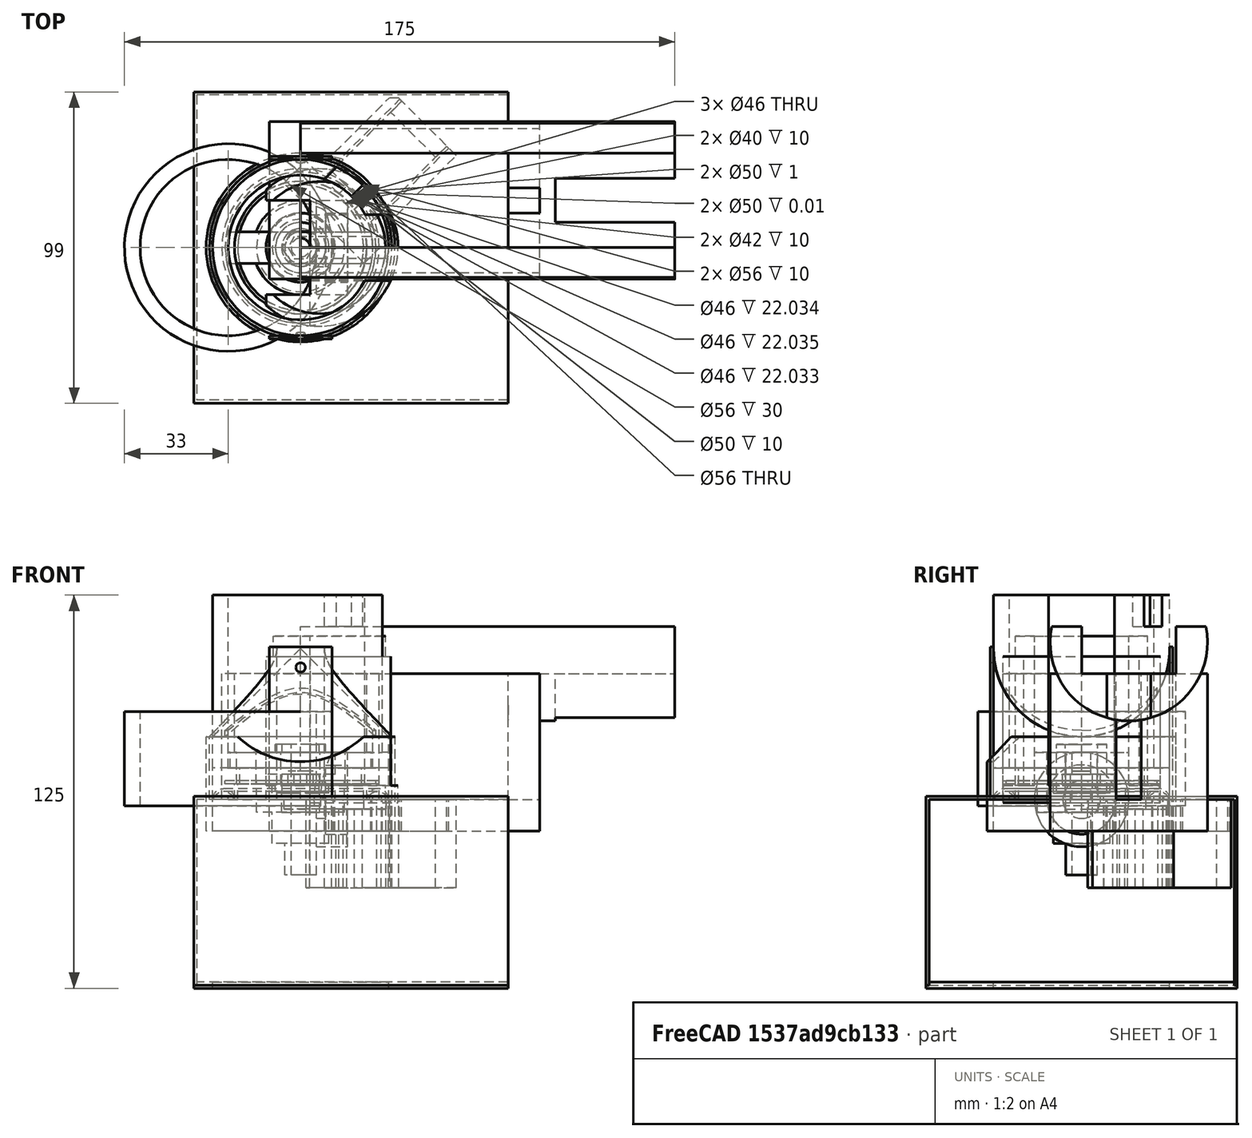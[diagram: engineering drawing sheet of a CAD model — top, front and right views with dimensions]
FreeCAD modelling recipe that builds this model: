
FCSTD DOCUMENT  (FreeCAD 0.18R16093 (Git))
Label: chess-robot-arm
License: All rights reserved
LicenseURL: http://en.wikipedia.org/wiki/All_rights_reserved
objects: Part::Cut×121, Part::Cylinder×116, Part::Box×52, Part::MultiFuse×35, App::DocumentObjectGroup×16, Part::RegularPolygon×9, Part::Extrusion×9, Part::MultiCommon×8, Part::Torus×7, App::MeasureDistance×2
note: 357 computed .brp shape members not serialized (recipe doc carries the construction recipe); baked Part::Feature solids carry a one-line shape summary decoded from their .brp

FEATURE [Part::Cylinder] Cylinder
  Angle = 360
  AttacherType = Attacher::AttachEngine3D
  Height = 10
  Radius = 29
FEATURE [Part::Torus] Torus
  Angle1 = -180
  Angle2 = 180
  Angle3 = 360
  AttacherType = Attacher::AttachEngine3D
  Placement = pos=(0,0,-1) rot=(0,0,1;0rad)
  Radius1 = 24.5
  Radius2 = 3.5
FEATURE [Part::Cut] Cut
  Base = -> Cylinder
  Tool = -> Torus
FEATURE [Part::Cylinder] Cylinder001
  Angle = 360
  AttacherType = Attacher::AttachEngine3D
  Height = 10
  Radius = 20
FEATURE [Part::Cut] Cut001
  Base = -> Cut
  Tool = -> Cylinder001
FEATURE [App::MeasureDistance] Distance  label="Distance: 87.82 mm"
  Distance = 87.8199
  P1 = (43.8613,-2.29371,0)
  P2 = (-43.9472,-0.873052,0)
FEATURE [App::MeasureDistance] Distance001  label="Distance: 10.00 mm"
  Distance = 10
  P1 = (30,0,0)
  P2 = (20,0,0)
FEATURE [Part::Cylinder] Cylinder002
  Angle = 360
  AttacherType = Attacher::AttachEngine3D
  Height = 10
  Radius = 23
FEATURE [Part::Box] Box  label="Cube"
  AttacherType = Attacher::AttachEngine3D
  Height = 10
  Length = 60
  Placement = pos=(-30,-5,0) rot=(0,0,1;0rad)
  Width = 10
FEATURE [Part::MultiCommon] Common  label="bolt-shaft"
  Shapes = -> [Box,Cylinder002]
FEATURE [Part::RegularPolygon] RegularPolygon  label="Regular polygon"
  AttacherType = Attacher::AttachEngine3D
  Circumradius = 6
  Polygon = 6
FEATURE [Part::Extrusion] Extrude  label="hex-head"
  Base = -> RegularPolygon
  Dir = (0,0,1)
  DirMode = 2
  FaceMakerClass = Part::FaceMakerBullseye
  LengthFwd = 3
  LengthRev = 0
  Solid = true
  Symmetric = false
FEATURE [Part::Cut] Cut002  label="bolt"
  Base = -> Common
  Tool = -> Extrude
FEATURE [Part::Cylinder] Cylinder003
  Angle = 360
  AttacherType = Attacher::AttachEngine3D
  Height = 10
  Radius = 3
FEATURE [Part::Cut] Cut003  label="center-axis001"
  Base = -> Cut002
  Placement = pos=(0,0,5) rot=(0,0,1;0rad)
  Tool = -> Cylinder003
FEATURE [Part::Cylinder] Cylinder004
  Angle = 360
  AttacherType = Attacher::AttachEngine3D
  Height = 0.01
  Placement = pos=(10,0,0) rot=(0,0,1;0rad)
  Radius = 24
FEATURE [Part::Cylinder] Cylinder005
  Angle = 360
  AttacherType = Attacher::AttachEngine3D
  Height = 0.01
  Placement = pos=(10,0,0) rot=(0,0,1;0rad)
  Radius = 25
FEATURE [Part::Cut] Cut004
  Base = -> Cylinder005
  Placement = pos=(-10,0,5) rot=(0,0,1;0rad)
  Tool = -> Cylinder004
FEATURE [Part::MultiFuse] Fusion
  Shapes = -> [Cut003,Cut001]
FEATURE [Part::Cut] Cut005  label="small-attachment001"
  Base = -> Fusion
  Tool = -> Cut004
FEATURE [Part::Torus] Torus001
  Angle1 = -180
  Angle2 = 180
  Angle3 = 360
  AttacherType = Attacher::AttachEngine3D
  Placement = pos=(0,0,-0.5) rot=(0,0,1;0rad)
  Radius1 = 24.5
  Radius2 = 3.5
FEATURE [Part::Cylinder] Cylinder006
  Angle = 360
  AttacherType = Attacher::AttachEngine3D
  Height = 10
  Radius = 20
FEATURE [Part::Cylinder] Cylinder007
  Angle = 360
  AttacherType = Attacher::AttachEngine3D
  Height = 10
  Radius = 29
FEATURE [Part::Cut] Cut007
  Base = -> Cylinder007
  Tool = -> Torus001
FEATURE [Part::Cut] Cut006
  Base = -> Cut007
  Tool = -> Cylinder006
FEATURE [Part::Cylinder] Cylinder008
  Angle = 360
  AttacherType = Attacher::AttachEngine3D
  Height = 1
  Placement = pos=(10,0,0) rot=(0,0,1;0rad)
  Radius = 25
FEATURE [Part::Cylinder] Cylinder009
  Angle = 360
  AttacherType = Attacher::AttachEngine3D
  Height = 10
  Radius = 23
FEATURE [Part::Box] Box001  label="Cube001"
  AttacherType = Attacher::AttachEngine3D
  Height = 10
  Length = 60
  Placement = pos=(-30,-5,0) rot=(0,0,1;0rad)
  Width = 10
FEATURE [Part::Cylinder] Cylinder010
  Angle = 360
  AttacherType = Attacher::AttachEngine3D
  Height = 5
  Placement = pos=(10,0,0) rot=(0,0,1;0rad)
  Radius = 24
FEATURE [Part::Cut] Cut008
  Base = -> Cylinder008
  Placement = pos=(-10,0,5) rot=(0,1,0;0rad)
  Tool = -> Cylinder010
FEATURE [Part::Cylinder] Cylinder011
  Angle = 360
  AttacherType = Attacher::AttachEngine3D
  Height = 10
  Radius = 3
FEATURE [Part::MultiCommon] Common001  label="bolt-shaft001"
  Shapes = -> [Box001,Cylinder009]
FEATURE [Part::RegularPolygon] RegularPolygon001  label="Regular polygon001"
  AttacherType = Attacher::AttachEngine3D
  Circumradius = 4
  Polygon = 6
FEATURE [Part::Extrusion] Extrude001  label="hex-head001"
  Base = -> RegularPolygon001
  Dir = (0,0,1)
  DirMode = 2
  FaceMakerClass = Part::FaceMakerBullseye
  LengthFwd = 4
  LengthRev = 0
  Solid = true
  Symmetric = false
FEATURE [Part::Cut] Cut011  label="bolt001"
  Base = -> Common001
  Tool = -> Extrude001
FEATURE [Part::Cut] Cut009  label="center-axis002"
  Base = -> Cut011
  Placement = pos=(0,0,5) rot=(0,0,1;0rad)
  Tool = -> Cylinder011
FEATURE [Part::MultiFuse] Fusion001
  Shapes = -> [Cut009,Cut006]
FEATURE [Part::Cut] Cut010
  Base = -> Fusion001
  Tool = -> Cut008
FEATURE [Part::Cylinder] Cylinder012  label="center-Cylinder012"
  Angle = 360
  AttacherType = Attacher::AttachEngine3D
  Height = 10
  Placement = pos=(0,0,5) rot=(0,0,1;0rad)
  Radius = 15
FEATURE [Part::Cylinder] Cylinder013
  Angle = 360
  AttacherType = Attacher::AttachEngine3D
  Height = 38
  Radius = 28
FEATURE [Part::Cylinder] Cylinder014
  Angle = 360
  AttacherType = Attacher::AttachEngine3D
  Height = 38
  Radius = 23
FEATURE [Part::Cut] Cut012
  Base = -> Cylinder013
  Tool = -> Cylinder014
FEATURE [Part::Cylinder] Cylinder015
  Angle = 360
  AttacherType = Attacher::AttachEngine3D
  Height = 61
  Placement = pos=(-29,0,38) rot=(0,1,0;1.5708rad)
  Radius = 28
FEATURE [Part::Cut] Cut013
  Base = -> Cut012
  Tool = -> Cylinder015
FEATURE [Part::Cylinder] Cylinder016
  Angle = 360
  AttacherType = Attacher::AttachEngine3D
  Height = 40
  Radius = 23
FEATURE [Part::Cylinder] Cylinder017
  Angle = 360
  AttacherType = Attacher::AttachEngine3D
  Height = 61
  Placement = pos=(-29,0,40) rot=(0,1,0;1.5708rad)
  Radius = 28
FEATURE [Part::Cylinder] Cylinder018
  Angle = 360
  AttacherType = Attacher::AttachEngine3D
  Height = 40
  Radius = 24
FEATURE [Part::Cut] Cut014
  Base = -> Cylinder018
  Tool = -> Cylinder016
FEATURE [Part::Cut] Cut015
  Base = -> Cut014
  Tool = -> Cylinder017
FEATURE [Part::MultiFuse] Fusion002
  Placement = pos=(0,0,10) rot=(0,0,1;0rad)
  Shapes = -> [Cut015,Cut013]
FEATURE [App::DocumentObjectGroup] Group002  label="Servo bend"
  Group = -> [Fusion002]
FEATURE [Part::Cylinder] Cylinder019
  Angle = 360
  AttacherType = Attacher::AttachEngine3D
  Height = 48
  Radius = 23
FEATURE [Part::Cylinder] Cylinder020
  Angle = 360
  AttacherType = Attacher::AttachEngine3D
  Height = 61
  Placement = pos=(-29,0,38) rot=(0,1,0;1.5708rad)
  Radius = 28
FEATURE [Part::Cylinder] Cylinder021
  Angle = 360
  AttacherType = Attacher::AttachEngine3D
  Height = 48
  Radius = 29
FEATURE [Part::Cut] Cut016
  Base = -> Cylinder021
  Tool = -> Cylinder019
FEATURE [Part::Cut] Cut017
  Base = -> Cut016
  Tool = -> Cylinder020
FEATURE [Part::Cylinder] Cylinder022
  Angle = 360
  AttacherType = Attacher::AttachEngine3D
  Height = 40
  Radius = 23
FEATURE [Part::Cylinder] Cylinder023
  Angle = 360
  AttacherType = Attacher::AttachEngine3D
  Height = 61
  Placement = pos=(-29,0,40) rot=(0,1,0;1.5708rad)
  Radius = 28
FEATURE [Part::Cylinder] Cylinder024
  Angle = 360
  AttacherType = Attacher::AttachEngine3D
  Height = 40
  Radius = 24
FEATURE [Part::Cut] Cut018
  Base = -> Cylinder024
  Tool = -> Cylinder022
FEATURE [Part::Cut] Cut019
  Base = -> Cut018
  Tool = -> Cylinder023
FEATURE [Part::MultiFuse] Fusion003
  Placement = pos=(0,0,10) rot=(0,0,1;0rad)
  Shapes = -> [Cut019,Cut017]
FEATURE [Part::MultiFuse] Fusion004
  Shapes = -> [Cylinder012,Cut010]
FEATURE [Part::MultiFuse] Fusion005
  Shapes = -> [Fusion004,Fusion003]
FEATURE [Part::Cylinder] Cylinder025  label="center-Cylinder025"
  Angle = 360
  AttacherType = Attacher::AttachEngine3D
  Height = 7
  Placement = pos=(0,0,8) rot=(0,0,1;0rad)
  Radius = 11
FEATURE [Part::Cut] Cut020
  Base = -> Fusion005
  Tool = -> Cylinder025
FEATURE [Part::Cylinder] Cylinder026  label="center-Cylinder026"
  Angle = 360
  AttacherType = Attacher::AttachEngine3D
  Height = 10
  Placement = pos=(0,0,5) rot=(0,0,1;0rad)
  Radius = 6
FEATURE [Part::Cut] Cut021
  Base = -> Cut020
  Tool = -> Cylinder026
FEATURE [Part::Cylinder] Cylinder027
  Angle = 360
  AttacherType = Attacher::AttachEngine3D
  Height = 45
  Radius = 23
FEATURE [Part::Cylinder] Cylinder028
  Angle = 360
  AttacherType = Attacher::AttachEngine3D
  Height = 61
  Placement = pos=(-29,0,38) rot=(0,1,0;1.5708rad)
  Radius = 28
FEATURE [Part::Cylinder] Cylinder029
  Angle = 360
  AttacherType = Attacher::AttachEngine3D
  Height = 45
  Radius = 29
FEATURE [Part::Cut] Cut022
  Base = -> Cylinder029
  Tool = -> Cylinder027
FEATURE [Part::Cut] Cut023
  Base = -> Cut022
  Tool = -> Cylinder028
FEATURE [Part::Cylinder] Cylinder030
  Angle = 360
  AttacherType = Attacher::AttachEngine3D
  Height = 40
  Radius = 23
FEATURE [Part::Cylinder] Cylinder031
  Angle = 360
  AttacherType = Attacher::AttachEngine3D
  Height = 61
  Placement = pos=(-29,0,40) rot=(0,1,0;1.5708rad)
  Radius = 28
FEATURE [Part::Cylinder] Cylinder032
  Angle = 360
  AttacherType = Attacher::AttachEngine3D
  Height = 40
  Radius = 24
FEATURE [Part::Cut] Cut024
  Base = -> Cylinder032
  Tool = -> Cylinder030
FEATURE [Part::Cut] Cut025
  Base = -> Cut024
  Tool = -> Cylinder031
FEATURE [Part::MultiFuse] Fusion006
  Placement = pos=(0,0,10) rot=(0,0,1;0rad)
  Shapes = -> [Cut025,Cut023]
FEATURE [Part::MultiFuse] Fusion007
  Shapes = -> [Fusion006,Cut005]
FEATURE [Part::Cylinder] Cylinder033
  Angle = 360
  AttacherType = Attacher::AttachEngine3D
  Height = 53
  Placement = pos=(6,0,-1) rot=(0,0,1;0rad)
  Radius = 25
FEATURE [Part::Box] Box002  label="Cube002"
  AttacherType = Attacher::AttachEngine3D
  Height = 41
  Length = 50
  Placement = pos=(-15,-10.5,4.5) rot=(0,0,1;0rad)
  Width = 21
FEATURE [Part::Cut] Cut026
  Base = -> Cylinder033
  Tool = -> Box002
FEATURE [Part::Box] Box003  label="Cube003"
  AttacherType = Attacher::AttachEngine3D
  Height = 71
  Length = 55
  Placement = pos=(-66,-25,-15) rot=(0,0,1;0rad)
  Width = 56
FEATURE [Part::Cut] Cut027
  Base = -> Cut026
  Tool = -> Box003
FEATURE [Part::Box] Box004  label="Cube004"
  AttacherType = Attacher::AttachEngine3D
  Height = 7
  Length = 24
  Placement = pos=(3,-3.5,-1) rot=(0,0,1;0rad)
  Width = 7
FEATURE [Part::Cut] Cut028
  Base = -> Cut027
  Tool = -> Box004
FEATURE [Part::Cylinder] Cylinder034
  Angle = 360
  AttacherType = Attacher::AttachEngine3D
  Height = 5
  Radius = 3
FEATURE [Part::Cylinder] Cylinder035
  Angle = 360
  AttacherType = Attacher::AttachEngine3D
  Height = 5
  Radius = 11
FEATURE [Part::Cut] Cut029
  Base = -> Cylinder035
  Tool = -> Cylinder034
FEATURE [Part::Cylinder] Cylinder036
  Angle = 360
  AttacherType = Attacher::AttachEngine3D
  Height = 10
  Placement = pos=(0,0,4.5) rot=(0,0,1;0rad)
  Radius = 10.6
FEATURE [Part::Cut] Cut030
  Base = -> Cut029
  Tool = -> Cylinder036
FEATURE [App::DocumentObjectGroup] Group004  label="shaft-coupler"
  Group = -> [Cut030]
FEATURE [Part::Torus] Torus002
  Angle1 = -180
  Angle2 = 180
  Angle3 = 360
  AttacherType = Attacher::AttachEngine3D
  Radius1 = 24.5
  Radius2 = 3.5
FEATURE [Part::RegularPolygon] RegularPolygon002  label="Regular polygon002"
  AttacherType = Attacher::AttachEngine3D
  Circumradius = 4
  Polygon = 6
FEATURE [Part::Cylinder] Cylinder037
  Angle = 360
  AttacherType = Attacher::AttachEngine3D
  Height = 10
  Radius = 28
FEATURE [Part::Cylinder] Cylinder038
  Angle = 360
  AttacherType = Attacher::AttachEngine3D
  Height = 10
  Radius = 21
FEATURE [Part::Box] Box005  label="Cube005"
  AttacherType = Attacher::AttachEngine3D
  Height = 10
  Length = 60
  Placement = pos=(-30,-5,0) rot=(0,0,1;0rad)
  Width = 10
FEATURE [Part::Cylinder] Cylinder039
  Angle = 360
  AttacherType = Attacher::AttachEngine3D
  Height = 0.01
  Placement = pos=(10,0,0) rot=(0,0,1;0rad)
  Radius = 25
FEATURE [Part::Cylinder] Cylinder040
  Angle = 360
  AttacherType = Attacher::AttachEngine3D
  Height = 0.01
  Placement = pos=(10,0,0) rot=(0,0,1;0rad)
  Radius = 24
FEATURE [Part::Cylinder] Cylinder041
  Angle = 360
  AttacherType = Attacher::AttachEngine3D
  Height = 10
  Radius = 23
FEATURE [Part::MultiCommon] Common002  label="bolt-shaft002"
  Shapes = -> [Box005,Cylinder041]
FEATURE [Part::Cylinder] Cylinder042
  Angle = 360
  AttacherType = Attacher::AttachEngine3D
  Height = 10
  Radius = 3
FEATURE [Part::Extrusion] Extrude002  label="hex-head002"
  Base = -> RegularPolygon002
  Dir = (0,0,1)
  DirMode = 2
  FaceMakerClass = Part::FaceMakerBullseye
  LengthFwd = 4
  LengthRev = 0
  Solid = true
  Symmetric = false
FEATURE [Part::Cut] Cut032
  Base = -> Cylinder039
  Placement = pos=(-10,0,5) rot=(0,0,1;0rad)
  Tool = -> Cylinder040
FEATURE [Part::Cut] Cut034
  Base = -> Cylinder037
  Tool = -> Torus002
FEATURE [Part::Cut] Cut031
  Base = -> Cut034
  Tool = -> Cylinder038
FEATURE [Part::Cut] Cut036  label="bolt002"
  Base = -> Common002
  Tool = -> Extrude002
FEATURE [Part::Cut] Cut033  label="center-axis003"
  Base = -> Cut036
  Placement = pos=(0,0,5) rot=(0,0,1;0rad)
  Tool = -> Cylinder042
FEATURE [Part::MultiFuse] Fusion008
  Shapes = -> [Cut033,Cut031]
FEATURE [Part::Cut] Cut035  label="small-attachment-base"
  Base = -> Fusion008
  Tool = -> Cut032
FEATURE [Part::Cylinder] Cylinder043
  Angle = 360
  AttacherType = Attacher::AttachEngine3D
  Height = 10
  Radius = 28
FEATURE [Part::Cylinder] Cylinder044
  Angle = 360
  AttacherType = Attacher::AttachEngine3D
  Height = 10
  Radius = 21
FEATURE [Part::Torus] Torus003
  Angle1 = -180
  Angle2 = 180
  Angle3 = 360
  AttacherType = Attacher::AttachEngine3D
  Radius1 = 24.5
  Radius2 = 3.5
FEATURE [Part::RegularPolygon] RegularPolygon003  label="Regular polygon003"
  AttacherType = Attacher::AttachEngine3D
  Circumradius = 4
  Polygon = 6
FEATURE [Part::Extrusion] Extrude003  label="hex-head003"
  Base = -> RegularPolygon003
  Dir = (0,0,1)
  DirMode = 2
  FaceMakerClass = Part::FaceMakerBullseye
  LengthFwd = 4
  LengthRev = 0
  Solid = true
  Symmetric = false
FEATURE [Part::Cut] Cut042
  Base = -> Cylinder043
  Tool = -> Torus003
FEATURE [Part::Cut] Cut041
  Base = -> Cut042
  Tool = -> Cylinder044
FEATURE [Part::Box] Box006  label="Cube006"
  AttacherType = Attacher::AttachEngine3D
  Height = 10
  Length = 60
  Placement = pos=(-30,-5,0) rot=(0,0,1;0rad)
  Width = 10
FEATURE [Part::Cylinder] Cylinder045
  Angle = 360
  AttacherType = Attacher::AttachEngine3D
  Height = 5
  Placement = pos=(10,0,0) rot=(0,0,1;0rad)
  Radius = 24
FEATURE [Part::Cylinder] Cylinder046
  Angle = 360
  AttacherType = Attacher::AttachEngine3D
  Height = 10
  Radius = 23
FEATURE [Part::MultiCommon] Common003  label="bolt-shaft003"
  Shapes = -> [Box006,Cylinder046]
FEATURE [Part::Cut] Cut040  label="bolt003"
  Base = -> Common003
  Tool = -> Extrude003
FEATURE [Part::Cylinder] Cylinder047
  Angle = 360
  AttacherType = Attacher::AttachEngine3D
  Height = 10
  Radius = 3
FEATURE [Part::Cut] Cut038  label="center-axis004"
  Base = -> Cut040
  Placement = pos=(0,0,5) rot=(0,0,1;0rad)
  Tool = -> Cylinder047
FEATURE [Part::MultiFuse] Fusion009
  Shapes = -> [Cut038,Cut041]
FEATURE [Part::Cylinder] Cylinder048
  Angle = 360
  AttacherType = Attacher::AttachEngine3D
  Height = 1
  Placement = pos=(10,0,0) rot=(0,0,1;0rad)
  Radius = 25
FEATURE [Part::Cut] Cut037
  Base = -> Cylinder048
  Placement = pos=(-10,0,5) rot=(0,1,0;0rad)
  Tool = -> Cylinder045
FEATURE [Part::Cut] Cut039
  Base = -> Fusion009
  Tool = -> Cut037
FEATURE [Part::Cylinder] Cylinder049  label="center-Cylinder027"
  Angle = 360
  AttacherType = Attacher::AttachEngine3D
  Height = 10
  Placement = pos=(0,0,5) rot=(0,0,1;0rad)
  Radius = 15
FEATURE [Part::MultiFuse] Fusion010
  Shapes = -> [Cylinder049,Cut039]
FEATURE [Part::Cylinder] Cylinder050  label="center-Cylinder028"
  Angle = 360
  AttacherType = Attacher::AttachEngine3D
  Height = 7
  Placement = pos=(0,0,8) rot=(0,0,1;0rad)
  Radius = 11
FEATURE [Part::Cylinder] Cylinder051  label="center-Cylinder029"
  Angle = 360
  AttacherType = Attacher::AttachEngine3D
  Height = 10
  Placement = pos=(0,0,5) rot=(0,0,1;0rad)
  Radius = 6
FEATURE [Part::Cut] Cut043
  Base = -> Fusion010
  Tool = -> Cylinder050
FEATURE [Part::Cut] Cut044  label="large-attachement-base"
  Base = -> Cut043
  Tool = -> Cylinder051
FEATURE [Part::Cylinder] Cylinder052  label="Cylinder049"
  Angle = 360
  AttacherType = Attacher::AttachEngine3D
  Height = 30
  Placement = pos=(0,0,10) rot=(0,0,1;0rad)
  Radius = 21
FEATURE [Part::Cylinder] Cylinder053  label="Cylinder050"
  Angle = 360
  AttacherType = Attacher::AttachEngine3D
  Height = 30
  Placement = pos=(0,0,10) rot=(0,0,1;0rad)
  Radius = 25
FEATURE [Part::Cut] Cut045
  Base = -> Cylinder053
  Tool = -> Cylinder052
FEATURE [Part::MultiFuse] Fusion011
  Shapes = -> [Cut035,Cut045]
FEATURE [App::DocumentObjectGroup] Group005  label="robot base coupler"
  Group = -> [Fusion011]
FEATURE [Part::Cylinder] Cylinder054  label="Cylinder051"
  Angle = 360
  AttacherType = Attacher::AttachEngine3D
  Height = 55
  Placement = pos=(0,0,10) rot=(0,0,1;0rad)
  Radius = 23
FEATURE [Part::Cylinder] Cylinder055  label="Cylinder052"
  Angle = 360
  AttacherType = Attacher::AttachEngine3D
  Height = 55
  Placement = pos=(0,0,10) rot=(0,0,1;0rad)
  Radius = 28
FEATURE [Part::Cut] Cut046  label="touch-bottom"
  Base = -> Cylinder055
  Tool = -> Cylinder054
FEATURE [Part::MultiFuse] Fusion012
  Shapes = -> [Cut046,Cut044]
FEATURE [Part::Box] Box007  label="servo inlet"
  AttacherType = Attacher::AttachEngine3D
  Height = 55
  Length = 35
  Placement = pos=(0,-10.5,15) rot=(0,0,1;0rad)
  Width = 21
FEATURE [Part::Cut] Cut047
  Base = -> Fusion012
  Tool = -> Box007
FEATURE [Part::Box] Box008  label="cabel inlet"
  AttacherType = Attacher::AttachEngine3D
  Height = 10
  Length = 18
  Placement = pos=(10,10,55) rot=(0,0,1;0.785398rad)
  Width = 10
FEATURE [Part::Cut] Cut048  label="base"
  Base = -> Cut047
  Tool = -> Box008
FEATURE [App::DocumentObjectGroup] Group006  label="robot base"
  Group = -> [Cut048]
FEATURE [Part::Torus] Torus004
  Angle1 = -180
  Angle2 = 180
  Angle3 = 360
  AttacherType = Attacher::AttachEngine3D
  Radius1 = 25.5
  Radius2 = 2.5
FEATURE [Part::Cylinder] Cylinder056
  Angle = 360
  AttacherType = Attacher::AttachEngine3D
  Height = 10
  Radius = 23
FEATURE [Part::Cylinder] Cylinder057
  Angle = 360
  AttacherType = Attacher::AttachEngine3D
  Height = 5
  Placement = pos=(10,0,0) rot=(0,0,1;0rad)
  Radius = 24
FEATURE [Part::Cylinder] Cylinder058
  Angle = 360
  AttacherType = Attacher::AttachEngine3D
  Height = 10
  Radius = 28
FEATURE [Part::Box] Box009  label="Cube007"
  AttacherType = Attacher::AttachEngine3D
  Height = 10
  Length = 60
  Placement = pos=(-30,-5,0) rot=(0,0,1;0rad)
  Width = 10
FEATURE [Part::MultiCommon] Common004  label="bolt-shaft004"
  Shapes = -> [Box009,Cylinder056]
FEATURE [Part::Cylinder] Cylinder059
  Angle = 360
  AttacherType = Attacher::AttachEngine3D
  Height = 10
  Radius = 23
FEATURE [Part::Cut] Cut051
  Base = -> Cylinder058
  Tool = -> Torus004
FEATURE [Part::Cut] Cut058
  Base = -> Cut051
  Tool = -> Cylinder059
FEATURE [Part::RegularPolygon] RegularPolygon004  label="Regular polygon004"
  AttacherType = Attacher::AttachEngine3D
  Circumradius = 4
  Polygon = 6
FEATURE [Part::Extrusion] Extrude004  label="hex-head004"
  Base = -> RegularPolygon004
  Dir = (0,0,1)
  DirMode = 2
  FaceMakerClass = Part::FaceMakerBullseye
  LengthFwd = 4
  LengthRev = 0
  Solid = true
  Symmetric = false
FEATURE [Part::Cut] Cut056  label="bolt004"
  Base = -> Common004
  Tool = -> Extrude004
FEATURE [Part::Cylinder] Cylinder060  label="center-Cylinder030"
  Angle = 360
  AttacherType = Attacher::AttachEngine3D
  Height = 10
  Placement = pos=(0,0,5) rot=(0,0,1;0rad)
  Radius = 6
FEATURE [Part::Cylinder] Cylinder061
  Angle = 360
  AttacherType = Attacher::AttachEngine3D
  Height = 1
  Placement = pos=(10,0,0) rot=(0,0,1;0rad)
  Radius = 25
FEATURE [Part::Cut] Cut059
  Base = -> Cylinder061
  Placement = pos=(-10,0,5) rot=(0,1,0;0rad)
  Tool = -> Cylinder057
FEATURE [Part::Cylinder] Cylinder062  label="Cylinder060"
  Angle = 360
  AttacherType = Attacher::AttachEngine3D
  Height = 55
  Placement = pos=(0,0,10) rot=(0,0,1;0rad)
  Radius = 23
FEATURE [Part::Cylinder] Cylinder063  label="Cylinder062"
  Angle = 360
  AttacherType = Attacher::AttachEngine3D
  Height = 55
  Placement = pos=(0,0,10) rot=(0,0,1;0rad)
  Radius = 28
FEATURE [Part::Cut] Cut050  label="touch-bottom001"
  Base = -> Cylinder063
  Tool = -> Cylinder062
FEATURE [Part::Box] Box010  label="servo inlet001"
  AttacherType = Attacher::AttachEngine3D
  Height = 55
  Length = 35
  Placement = pos=(0,-10.5,15) rot=(0,0,1;0rad)
  Width = 21
FEATURE [Part::Box] Box011  label="cabel inlet001"
  AttacherType = Attacher::AttachEngine3D
  Height = 10
  Length = 18
  Placement = pos=(10,10,55) rot=(0,0,1;0.785398rad)
  Width = 10
FEATURE [Part::Cylinder] Cylinder064
  Angle = 360
  AttacherType = Attacher::AttachEngine3D
  Height = 10
  Radius = 3
FEATURE [Part::Cut] Cut054  label="center-axis005"
  Base = -> Cut056
  Placement = pos=(0,0,5) rot=(0,0,1;0rad)
  Tool = -> Cylinder064
FEATURE [Part::MultiFuse] Fusion014
  Shapes = -> [Cut054,Cut058]
FEATURE [Part::Cut] Cut055
  Base = -> Fusion014
  Tool = -> Cut059
FEATURE [Part::Cylinder] Cylinder065  label="center-Cylinder031"
  Angle = 360
  AttacherType = Attacher::AttachEngine3D
  Height = 10
  Placement = pos=(0,0,5) rot=(0,0,1;0rad)
  Radius = 15
FEATURE [Part::MultiFuse] Fusion013
  Shapes = -> [Cylinder065,Cut055]
FEATURE [Part::Cylinder] Cylinder066  label="center-Cylinder032"
  Angle = 360
  AttacherType = Attacher::AttachEngine3D
  Height = 7
  Placement = pos=(0,0,8) rot=(0,0,1;0rad)
  Radius = 11
FEATURE [Part::Cut] Cut057
  Base = -> Fusion013
  Tool = -> Cylinder066
FEATURE [Part::Cut] Cut049  label="large-attachement-base001"
  Base = -> Cut057
  Tool = -> Cylinder060
FEATURE [Part::MultiFuse] Fusion015
  Shapes = -> [Cut050,Cut049]
FEATURE [Part::Cut] Cut052
  Base = -> Fusion015
  Tool = -> Box010
FEATURE [Part::Cut] Cut053  label="base001"
  Base = -> Cut052
  Placement = pos=(0,0,-63) rot=(0,0,1;0.785398rad)
  Tool = -> Box011
FEATURE [Part::Box] Box012  label="base-bottom"
  AttacherType = Attacher::AttachEngine3D
  Height = 1
  Length = 100
  Placement = pos=(-34,-49.5,0) rot=(0,0,1;0rad)
  Width = 99
  expr: Length = 100
FEATURE [Part::Box] Box013  label="Cube009"
  AttacherType = Attacher::AttachEngine3D
  Height = 10
  Length = 40
  Placement = pos=(20,5.8,-10) rot=(0,0,1;0.785398rad)
  Width = 20.2
FEATURE [Part::Box] Box014  label="Cube010"
  AttacherType = Attacher::AttachEngine3D
  Height = 10
  Length = 34
  Placement = pos=(23,7.5,-10) rot=(0,0,1;0.785398rad)
  Width = 22
FEATURE [Part::Cut] Cut060  label="servo-secure"
  Base = -> Box014
  Tool = -> Box013
FEATURE [Part::MultiFuse] Fusion016  label="bottom"
  Shapes = -> [Box012,Cut060]
FEATURE [Part::Box] Box015  label="face"
  AttacherType = Attacher::AttachEngine3D
  Height = 60
  Length = 100
  Placement = pos=(-34,48.5,-59) rot=(0,0,1;0rad)
  Width = 1
FEATURE [Part::Cut] Cut061  label="bottom001"
  Base = -> Fusion016
  Tool = -> Cut053
FEATURE [Part::Box] Box016  label="face001"
  AttacherType = Attacher::AttachEngine3D
  Height = 60
  Length = 99
  Placement = pos=(-33,-49.5,-59) rot=(0,0,1;1.5708rad)
  Width = 1
FEATURE [Part::Box] Box017  label="face002"
  AttacherType = Attacher::AttachEngine3D
  Height = 60
  Length = 100
  Placement = pos=(-34,-49.5,-59) rot=(0,0,1;0rad)
  Width = 1
FEATURE [Part::MultiFuse] Fusion017
  Shapes = -> [Cut061,Box015,Box016,Box017]
FEATURE [App::DocumentObjectGroup] Group007  label="robot base shell"
  Group = -> [Fusion017]
FEATURE [Part::Box] Box018  label="top"
  AttacherType = Attacher::AttachEngine3D
  Height = 2
  Length = 100
  Placement = pos=(-34,-49.5,-60) rot=(0,0,1;0rad)
  Width = 99
  expr: Length = 100
FEATURE [Part::Cylinder] Cylinder067
  Angle = 360
  AttacherType = Attacher::AttachEngine3D
  Height = 10
  Radius = 23
FEATURE [Part::Cylinder] Cylinder068  label="center-Cylinder033"
  Angle = 360
  AttacherType = Attacher::AttachEngine3D
  Height = 7
  Placement = pos=(0,0,8) rot=(0,0,1;0rad)
  Radius = 11
FEATURE [Part::Cylinder] Cylinder069  label="center-Cylinder034"
  Angle = 360
  AttacherType = Attacher::AttachEngine3D
  Height = 10
  Placement = pos=(0,0,5) rot=(0,0,1;0rad)
  Radius = 6
FEATURE [Part::Box] Box019  label="cabel inlet002"
  AttacherType = Attacher::AttachEngine3D
  Height = 10
  Length = 18
  Placement = pos=(10,10,55) rot=(0,0,1;0.785398rad)
  Width = 10
FEATURE [Part::Cylinder] Cylinder070  label="Cylinder069"
  Angle = 360
  AttacherType = Attacher::AttachEngine3D
  Height = 55
  Placement = pos=(0,0,10) rot=(0,0,1;0rad)
  Radius = 23
FEATURE [Part::Box] Box020  label="servo inlet002"
  AttacherType = Attacher::AttachEngine3D
  Height = 55
  Length = 35
  Placement = pos=(0,-10.5,15) rot=(0,0,1;0rad)
  Width = 21
FEATURE [Part::Cylinder] Cylinder071
  Angle = 360
  AttacherType = Attacher::AttachEngine3D
  Height = 1
  Placement = pos=(10,0,0) rot=(0,0,1;0rad)
  Radius = 25
FEATURE [Part::Cylinder] Cylinder072
  Angle = 360
  AttacherType = Attacher::AttachEngine3D
  Height = 10
  Radius = 3
FEATURE [Part::Cylinder] Cylinder073  label="Cylinder070"
  Angle = 360
  AttacherType = Attacher::AttachEngine3D
  Height = 55
  Placement = pos=(0,0,10) rot=(0,0,1;0rad)
  Radius = 28
FEATURE [Part::Cut] Cut067  label="touch-bottom002"
  Base = -> Cylinder073
  Tool = -> Cylinder070
FEATURE [Part::Cylinder] Cylinder074  label="center-Cylinder035"
  Angle = 360
  AttacherType = Attacher::AttachEngine3D
  Height = 10
  Placement = pos=(0,0,5) rot=(0,0,1;0rad)
  Radius = 15
FEATURE [Part::Cylinder] Cylinder075
  Angle = 360
  AttacherType = Attacher::AttachEngine3D
  Height = 10
  Radius = 28
FEATURE [Part::Box] Box021  label="Cube011"
  AttacherType = Attacher::AttachEngine3D
  Height = 10
  Length = 60
  Placement = pos=(-30,-5,0) rot=(0,0,1;0rad)
  Width = 10
FEATURE [Part::Cylinder] Cylinder076
  Angle = 360
  AttacherType = Attacher::AttachEngine3D
  Height = 5
  Placement = pos=(10,0,0) rot=(0,0,1;0rad)
  Radius = 24
FEATURE [Part::Cut] Cut072
  Base = -> Cylinder071
  Placement = pos=(-10,0,5) rot=(0,1,0;0rad)
  Tool = -> Cylinder076
FEATURE [Part::Cylinder] Cylinder077
  Angle = 360
  AttacherType = Attacher::AttachEngine3D
  Height = 10
  Radius = 23
FEATURE [Part::MultiCommon] Common005  label="bolt-shaft005"
  Shapes = -> [Box021,Cylinder077]
FEATURE [Part::Torus] Torus005
  Angle1 = -180
  Angle2 = 180
  Angle3 = 360
  AttacherType = Attacher::AttachEngine3D
  Radius1 = 25.5
  Radius2 = 2.5
FEATURE [Part::Cut] Cut069
  Base = -> Cylinder075
  Tool = -> Torus005
FEATURE [Part::Cut] Cut064
  Base = -> Cut069
  Tool = -> Cylinder067
FEATURE [Part::RegularPolygon] RegularPolygon005  label="Regular polygon005"
  AttacherType = Attacher::AttachEngine3D
  Circumradius = 4
  Polygon = 6
FEATURE [Part::Extrusion] Extrude005  label="hex-head005"
  Base = -> RegularPolygon005
  Dir = (0,0,1)
  DirMode = 2
  FaceMakerClass = Part::FaceMakerBullseye
  LengthFwd = 4
  LengthRev = 0
  Solid = true
  Symmetric = false
FEATURE [Part::Cut] Cut062  label="bolt005"
  Base = -> Common005
  Tool = -> Extrude005
FEATURE [Part::Cut] Cut066  label="center-axis006"
  Base = -> Cut062
  Placement = pos=(0,0,5) rot=(0,0,1;0rad)
  Tool = -> Cylinder072
FEATURE [Part::MultiFuse] Fusion018
  Shapes = -> [Cut066,Cut064]
FEATURE [Part::Cut] Cut071
  Base = -> Fusion018
  Tool = -> Cut072
FEATURE [Part::MultiFuse] Fusion020
  Shapes = -> [Cylinder074,Cut071]
FEATURE [Part::Cut] Cut063
  Base = -> Fusion020
  Tool = -> Cylinder068
FEATURE [Part::Cut] Cut065  label="large-attachement-base002"
  Base = -> Cut063
  Tool = -> Cylinder069
FEATURE [Part::MultiFuse] Fusion019
  Shapes = -> [Cut067,Cut065]
FEATURE [Part::Cut] Cut068
  Base = -> Fusion019
  Tool = -> Box020
FEATURE [Part::Cut] Cut070  label="base002"
  Base = -> Cut068
  Placement = pos=(0,0,-63) rot=(0,0,1;0.785398rad)
  Tool = -> Box019
FEATURE [Part::Box] Box022  label="face003"
  AttacherType = Attacher::AttachEngine3D
  Height = 60
  Length = 100
  Placement = pos=(-34,-49.5,-59) rot=(0,0,1;0rad)
  Width = 1
FEATURE [Part::Box] Box023  label="face004"
  AttacherType = Attacher::AttachEngine3D
  Height = 60
  Length = 99
  Placement = pos=(-33,-49.5,-59) rot=(0,0,1;1.5708rad)
  Width = 1
FEATURE [Part::Box] Box024  label="Cube012"
  AttacherType = Attacher::AttachEngine3D
  Height = 10
  Length = 40
  Placement = pos=(20,5.8,-10) rot=(0,0,1;0.785398rad)
  Width = 20.2
FEATURE [Part::Box] Box025  label="Cube013"
  AttacherType = Attacher::AttachEngine3D
  Height = 10
  Length = 34
  Placement = pos=(23,7.5,-10) rot=(0,0,1;0.785398rad)
  Width = 22
FEATURE [Part::Cut] Cut073  label="servo-secure001"
  Base = -> Box025
  Tool = -> Box024
FEATURE [Part::Box] Box026  label="base-bottom001"
  AttacherType = Attacher::AttachEngine3D
  Height = 1
  Length = 100
  Placement = pos=(-34,-49.5,0) rot=(0,0,1;0rad)
  Width = 99
  expr: Length = 100
FEATURE [Part::MultiFuse] Fusion021  label="bottom002"
  Shapes = -> [Box026,Cut073]
FEATURE [Part::Cut] Cut074  label="bottom003"
  Base = -> Fusion021
  Tool = -> Cut070
FEATURE [Part::Box] Box027  label="face005"
  AttacherType = Attacher::AttachEngine3D
  Height = 60
  Length = 100
  Placement = pos=(-34,48.5,-59) rot=(0,0,1;0rad)
  Width = 1
FEATURE [Part::MultiFuse] Fusion022
  Shapes = -> [Cut074,Box027,Box023,Box022]
FEATURE [Part::Cut] Cut075
  Base = -> Box018
  Tool = -> Fusion022
FEATURE [Part::Cylinder] Cylinder078
  Angle = 360
  AttacherType = Attacher::AttachEngine3D
  Height = 10
  Radius = 23
FEATURE [Part::Cylinder] Cylinder079  label="center-Cylinder036"
  Angle = 360
  AttacherType = Attacher::AttachEngine3D
  Height = 7
  Placement = pos=(0,0,8) rot=(0,0,1;0rad)
  Radius = 11
FEATURE [Part::Cylinder] Cylinder080  label="center-Cylinder037"
  Angle = 360
  AttacherType = Attacher::AttachEngine3D
  Height = 10
  Placement = pos=(0,0,5) rot=(0,0,1;0rad)
  Radius = 6
FEATURE [Part::Box] Box028  label="cabel inlet003"
  AttacherType = Attacher::AttachEngine3D
  Height = 10
  Length = 18
  Placement = pos=(10,10,55) rot=(0,0,1;0.785398rad)
  Width = 10
FEATURE [Part::Cylinder] Cylinder081  label="Cylinder080"
  Angle = 360
  AttacherType = Attacher::AttachEngine3D
  Height = 55
  Placement = pos=(0,0,10) rot=(0,0,1;0rad)
  Radius = 23
FEATURE [Part::Box] Box029  label="servo inlet003"
  AttacherType = Attacher::AttachEngine3D
  Height = 55
  Length = 35
  Placement = pos=(0,-10.5,15) rot=(0,0,1;0rad)
  Width = 21
FEATURE [Part::Cylinder] Cylinder082
  Angle = 360
  AttacherType = Attacher::AttachEngine3D
  Height = 1
  Placement = pos=(10,0,0) rot=(0,0,1;0rad)
  Radius = 25
FEATURE [Part::Cylinder] Cylinder083
  Angle = 360
  AttacherType = Attacher::AttachEngine3D
  Height = 10
  Radius = 3
FEATURE [Part::Cylinder] Cylinder084  label="Cylinder081"
  Angle = 360
  AttacherType = Attacher::AttachEngine3D
  Height = 55
  Placement = pos=(0,0,10) rot=(0,0,1;0rad)
  Radius = 28
FEATURE [Part::Cut] Cut081  label="touch-bottom003"
  Base = -> Cylinder084
  Tool = -> Cylinder081
FEATURE [Part::Cylinder] Cylinder085  label="center-Cylinder038"
  Angle = 360
  AttacherType = Attacher::AttachEngine3D
  Height = 10
  Placement = pos=(0,0,5) rot=(0,0,1;0rad)
  Radius = 15
FEATURE [Part::Cylinder] Cylinder086
  Angle = 360
  AttacherType = Attacher::AttachEngine3D
  Height = 10
  Radius = 28
FEATURE [Part::Box] Box030  label="Cube014"
  AttacherType = Attacher::AttachEngine3D
  Height = 10
  Length = 60
  Placement = pos=(-30,-5,0) rot=(0,0,1;0rad)
  Width = 10
FEATURE [Part::Cylinder] Cylinder087
  Angle = 360
  AttacherType = Attacher::AttachEngine3D
  Height = 5
  Placement = pos=(10,0,0) rot=(0,0,1;0rad)
  Radius = 24
FEATURE [Part::Cut] Cut086
  Base = -> Cylinder082
  Placement = pos=(-10,0,5) rot=(0,1,0;0rad)
  Tool = -> Cylinder087
FEATURE [Part::Cylinder] Cylinder088
  Angle = 360
  AttacherType = Attacher::AttachEngine3D
  Height = 10
  Radius = 23
FEATURE [Part::MultiCommon] Common006  label="bolt-shaft006"
  Shapes = -> [Box030,Cylinder088]
FEATURE [Part::Torus] Torus006
  Angle1 = -180
  Angle2 = 180
  Angle3 = 360
  AttacherType = Attacher::AttachEngine3D
  Radius1 = 25.5
  Radius2 = 2.5
FEATURE [Part::Cut] Cut083
  Base = -> Cylinder086
  Tool = -> Torus006
FEATURE [Part::Cut] Cut078
  Base = -> Cut083
  Tool = -> Cylinder078
FEATURE [Part::RegularPolygon] RegularPolygon006  label="Regular polygon006"
  AttacherType = Attacher::AttachEngine3D
  Circumradius = 4
  Polygon = 6
FEATURE [Part::Extrusion] Extrude006  label="hex-head006"
  Base = -> RegularPolygon006
  Dir = (0,0,1)
  DirMode = 2
  FaceMakerClass = Part::FaceMakerBullseye
  LengthFwd = 4
  LengthRev = 0
  Solid = true
  Symmetric = false
FEATURE [Part::Cut] Cut076  label="bolt006"
  Base = -> Common006
  Tool = -> Extrude006
FEATURE [Part::Cut] Cut080  label="center-axis007"
  Base = -> Cut076
  Placement = pos=(0,0,5) rot=(0,0,1;0rad)
  Tool = -> Cylinder083
FEATURE [Part::MultiFuse] Fusion023
  Shapes = -> [Cut080,Cut078]
FEATURE [Part::Cut] Cut085
  Base = -> Fusion023
  Tool = -> Cut086
FEATURE [Part::MultiFuse] Fusion025
  Shapes = -> [Cylinder085,Cut085]
FEATURE [Part::Cut] Cut077
  Base = -> Fusion025
  Tool = -> Cylinder079
FEATURE [Part::Cut] Cut079  label="large-attachement-base003"
  Base = -> Cut077
  Tool = -> Cylinder080
FEATURE [Part::MultiFuse] Fusion024
  Shapes = -> [Cut081,Cut079]
FEATURE [Part::Cut] Cut082
  Base = -> Fusion024
  Tool = -> Box029
FEATURE [Part::Cut] Cut084  label="base003"
  Base = -> Cut082
  Placement = pos=(0,0,-63) rot=(0,0,1;0.785398rad)
  Tool = -> Box028
FEATURE [Part::Cut] Cut087
  Base = -> Cut075
  Tool = -> Cut084
FEATURE [Part::Cylinder] Cylinder089
  Angle = 360
  AttacherType = Attacher::AttachEngine3D
  Height = 10
  Placement = pos=(0,0,-63) rot=(0,0,1;0rad)
  Radius = 25
FEATURE [Part::Cut] Cut088  label="top001"
  Base = -> Cut087
  Tool = -> Cylinder089
FEATURE [App::DocumentObjectGroup] Group008  label="robot base top shell"
  Group = -> [Cut088]
FEATURE [Part::Box] Box031  label="Cube015"
  AttacherType = Attacher::AttachEngine3D
  Height = 53
  Length = 14
  Placement = pos=(-11,-15,-1) rot=(0,0,1;0rad)
  Width = 30
FEATURE [Part::Cut] Cut089
  Base = -> Cut028
  Tool = -> Box031
FEATURE [Part::Box] Box032  label="Cube016"
  AttacherType = Attacher::AttachEngine3D
  Height = 5.5
  Length = 14
  Placement = pos=(-11,-25,-1) rot=(0,0,1;0rad)
  Width = 50
FEATURE [Part::Cut] Cut090
  Base = -> Cut089
  Tool = -> Box032
FEATURE [Part::Box] Box033  label="inner"
  AttacherType = Attacher::AttachEngine3D
  Height = 28
  Length = 26.5
  Placement = pos=(24.2,10,-28) rot=(0,0,1;0.785398rad)
  Width = 20.2
FEATURE [Part::Box] Box034  label="outer"
  AttacherType = Attacher::AttachEngine3D
  Height = 28
  Length = 31.5
  Placement = pos=(27.2,7,-28) rot=(0,0,1;0.785398rad)
  Width = 28
FEATURE [Part::Cut] Cut091  label="main-container-hold"
  Base = -> Box034
  Tool = -> Box033
FEATURE [Part::Box] Box035  label="Cube017"
  AttacherType = Attacher::AttachEngine3D
  Height = 10
  Length = 40
  Placement = pos=(20,5.8,-10) rot=(0,0,1;0.785398rad)
  Width = 20.2
FEATURE [Part::Box] Box036  label="Cube018"
  AttacherType = Attacher::AttachEngine3D
  Height = 10
  Length = 34
  Placement = pos=(23,7.5,-10) rot=(0,0,1;0.785398rad)
  Width = 22
FEATURE [Part::Cut] Cut092  label="servo-secure002"
  Base = -> Box036
  Tool = -> Box035
FEATURE [Part::Cut] Cut093
  Base = -> Cut091
  Tool = -> Cut092
FEATURE [Part::Cylinder] Cylinder090
  Angle = 360
  AttacherType = Attacher::AttachEngine3D
  Height = 28
  Placement = pos=(0,0,-28) rot=(0,0,1;0rad)
  Radius = 28
FEATURE [Part::Cut] Cut094
  Base = -> Cut093
  Tool = -> Cylinder090
FEATURE [Part::Box] Box037  label="face006"
  AttacherType = Attacher::AttachEngine3D
  Height = 60
  Length = 100
  Placement = pos=(-33,47.5,-59) rot=(0,0,1;0rad)
  Width = 2
FEATURE [Part::Cut] Cut095
  Base = -> Cut094
  Tool = -> Box037
FEATURE [Part::Cylinder] Cylinder091
  Angle = 360
  AttacherType = Attacher::AttachEngine3D
  Height = 6.5
  Placement = pos=(6,0,45.5) rot=(0,0,1;0rad)
  Radius = 21
FEATURE [Part::Cylinder] Cylinder092
  Angle = 360
  AttacherType = Attacher::AttachEngine3D
  Height = 6.5
  Placement = pos=(6,0,45.5) rot=(0,0,1;0rad)
  Radius = 25
FEATURE [Part::Cut] Cut096
  Base = -> Cylinder092
  Tool = -> Cylinder091
FEATURE [Part::Cut] Cut097
  Base = -> Cut090
  Tool = -> Cut096
FEATURE [App::DocumentObjectGroup] Group003  label="servo hold"
  Group = -> [Cut097]
FEATURE [Part::Box] Box038  label="Cube019"
  AttacherType = Attacher::AttachEngine3D
  Height = 28
  Length = 60
  Placement = pos=(-31,-31,48.5) rot=(0,0,1;0rad)
  Width = 60
FEATURE [Part::Cut] Cut098  label="main"
  Base = -> Fusion007
  Tool = -> Box038
FEATURE [Part::Box] Box039  label="Cube020"
  AttacherType = Attacher::AttachEngine3D
  Height = 28
  Length = 60
  Placement = pos=(-31,-31,48.5) rot=(0,0,1;0rad)
  Width = 60
FEATURE [Part::Cut] Cut099
  Base = -> Cut021
  Tool = -> Box039
FEATURE [Part::Cylinder] Cylinder093
  Angle = 360
  AttacherType = Attacher::AttachEngine3D
  Height = 15
  Placement = pos=(0,0,5) rot=(0,0,1;0rad)
  Radius = 8
FEATURE [Part::RegularPolygon] RegularPolygon007  label="Regular polygon007"
  AttacherType = Attacher::AttachEngine3D
  Circumradius = 5.9
  Polygon = 6
FEATURE [Part::Extrusion] Extrude007  label="hex-head007"
  Base = -> RegularPolygon007
  Dir = (0,0,1)
  DirMode = 2
  FaceMakerClass = Part::FaceMakerBullseye
  LengthFwd = 15
  LengthRev = 0
  Placement = pos=(0,0,5) rot=(0,0,1;0rad)
  Solid = true
  Symmetric = false
FEATURE [Part::Cut] Cut100  label="hex-nut-secure"
  Base = -> Cylinder093
  Placement = pos=(0,0,-2.5) rot=(0,0,1;0rad)
  Tool = -> Extrude007
FEATURE [Part::MultiFuse] Fusion026
  Shapes = -> [Cut100,Cut098]
FEATURE [App::DocumentObjectGroup] Group  label="small-attachment"
  Group = -> [Fusion026]
FEATURE [Part::Box] Box040  label="Cube021"
  AttacherType = Attacher::AttachEngine3D
  Height = 48.5
  Length = 20
  Placement = pos=(-10,-29,0) rot=(0,0,1;0rad)
  Width = 1
FEATURE [Part::Box] Box041  label="Cube022"
  AttacherType = Attacher::AttachEngine3D
  Height = 48.5
  Length = 20
  Placement = pos=(-10,28,0) rot=(0,0,1;0rad)
  Width = 1
FEATURE [Part::Cylinder] Cylinder094
  Angle = 360
  AttacherType = Attacher::AttachEngine3D
  Height = 60
  Placement = pos=(0,30,42) rot=(1,0,0;1.5708rad)
  Radius = 1.5
FEATURE [Part::MultiFuse] Fusion027  label="side-reinforcements"
  Shapes = -> [Box041,Box040]
FEATURE [Part::MultiFuse] Fusion028
  Shapes = -> [Fusion027,Cut099]
FEATURE [Part::Cut] Cut101
  Base = -> Fusion028
  Tool = -> Cylinder094
FEATURE [App::DocumentObjectGroup] Group001  label="large-attachment"
  Group = -> [Cut101]
FEATURE [Part::Cylinder] Cylinder095
  Angle = 360
  AttacherType = Attacher::AttachEngine3D
  Height = 10
  Radius = 25
FEATURE [Part::Cylinder] Cylinder096
  Angle = 360
  AttacherType = Attacher::AttachEngine3D
  Height = 10
  Radius = 28
FEATURE [Part::Cut] Cut102
  Base = -> Cylinder096
  Tool = -> Cylinder095
FEATURE [Part::Cylinder] Cylinder097
  Angle = 360
  AttacherType = Attacher::AttachEngine3D
  Height = 30
  Placement = pos=(0,0,-10) rot=(0,0,1;0rad)
  Radius = 28
FEATURE [Part::Cylinder] Cylinder098
  Angle = 360
  AttacherType = Attacher::AttachEngine3D
  Height = 30
  Placement = pos=(0,0,-10) rot=(0,0,1;0rad)
  Radius = 30
FEATURE [Part::Cut] Cut103
  Base = -> Cylinder098
  Tool = -> Cylinder097
FEATURE [Part::Cylinder] Cylinder099
  Angle = 360
  AttacherType = Attacher::AttachEngine3D
  Height = 46
  Placement = pos=(0,0,41) rot=(1,0,0;1.5708rad)
  Radius = 29
FEATURE [Part::MultiFuse] Fusion029
  Shapes = -> [Cut102,Cut103]
FEATURE [Part::Cut] Cut104
  Base = -> Fusion029
  Tool = -> Cylinder099
FEATURE [App::DocumentObjectGroup] Group010  label="arm-extender"
  Group = -> [Cut104]
FEATURE [Part::Cylinder] Cylinder100
  Angle = 360
  AttacherType = Attacher::AttachEngine3D
  Height = 28
  Placement = pos=(7,7,-28) rot=(0,0,1;0rad)
  Radius = 22
FEATURE [App::DocumentObjectGroup] Group011  label="outside"
  Group = -> [Cut095]
FEATURE [Part::Box] Box042  label="inner001"
  AttacherType = Attacher::AttachEngine3D
  Height = 28
  Length = 26.5
  Placement = pos=(24.2,10,-28) rot=(0,0,1;0.785398rad)
  Width = 20.2
FEATURE [Part::Box] Box043  label="outer001"
  AttacherType = Attacher::AttachEngine3D
  Height = 28
  Length = 16.5
  Placement = pos=(27.2,2,-28) rot=(0,0,1;0.785398rad)
  Width = 36
FEATURE [Part::Cut] Cut105  label="main-container-hold001"
  Base = -> Box043
  Tool = -> Box042
FEATURE [Part::Box] Box044  label="Cube023"
  AttacherType = Attacher::AttachEngine3D
  Height = 25
  Length = 4
  Placement = pos=(17,12,-28) rot=(0,0,1;0.785398rad)
  Width = 7
FEATURE [Part::Box] Box045  label="Cube024"
  AttacherType = Attacher::AttachEngine3D
  Height = 3
  Length = 10
  Placement = pos=(20.19,-5,-3) rot=(0,0,1;0.785398rad)
  Width = 36
FEATURE [Part::MultiCommon] Common007
  Shapes = -> [Cut105,Cylinder100]
FEATURE [Part::Cut] Cut106
  Base = -> Common007
  Tool = -> Box044
FEATURE [Part::MultiFuse] Fusion030
  Shapes = -> [Box045,Cut106]
FEATURE [App::DocumentObjectGroup] Group012  label="inside"
  Group = -> [Fusion030]
FEATURE [App::DocumentObjectGroup] Group009  label="base-servo-hold"
  Group = -> [Group011,Group012]
FEATURE [Part::Box] Box046  label="Cube025"
  AttacherType = Attacher::AttachEngine3D
  Height = 60
  Length = 66
  Width = 30
FEATURE [Part::Box] Box047  label="Cube026"
  AttacherType = Attacher::AttachEngine3D
  Height = 50
  Length = 86
  Placement = pos=(-10,-10,-10) rot=(0,0,1;0rad)
  Width = 50
FEATURE [Part::Cut] Cut107
  Base = -> Box047
  Tool = -> Box046
FEATURE [Part::Cylinder] Cylinder101
  Angle = 360
  AttacherType = Attacher::AttachEngine3D
  Height = 119
  Placement = pos=(0,15,50) rot=(0,1,0;1.5708rad)
  Radius = 25
FEATURE [Part::Cut] Cut108
  Base = -> Cylinder101
  Tool = -> Box046
FEATURE [Part::Box] Box048  label="Cube027"
  AttacherType = Attacher::AttachEngine3D
  Height = 30
  Length = 119
  Placement = pos=(0,-13,55) rot=(0,0,1;0rad)
  Width = 70
FEATURE [Part::Cut] Cut109
  Base = -> Cut108
  Tool = -> Box048
FEATURE [Part::Box] Box049  label="Cube028"
  AttacherType = Attacher::AttachEngine3D
  Height = 15
  Length = 67
  Placement = pos=(66,0,40) rot=(0,0,1;0rad)
  Width = 30
FEATURE [Part::Cut] Cut110
  Base = -> Cut109
  Tool = -> Box049
FEATURE [Part::Box] Box050  label="Cube029"
  AttacherType = Attacher::AttachEngine3D
  Height = 25
  Length = 67
  Placement = pos=(81,8,15) rot=(0,0,1;0rad)
  Width = 14
FEATURE [Part::Cut] Cut111
  Base = -> Cut110
  Tool = -> Box050
FEATURE [Part::Box] Box051  label="Cube030"
  AttacherType = Attacher::AttachEngine3D
  Height = 40
  Length = 10
  Placement = pos=(66,11,0) rot=(0,0,1;0rad)
  Width = 8
FEATURE [Part::MultiFuse] Fusion031
  Shapes = -> [Cut107,Cut111]
FEATURE [Part::Cut] Cut112
  Base = -> Fusion031
  Tool = -> Box051
FEATURE [App::DocumentObjectGroup] Group013  label="60KG-Servo-hold"
  Group = -> [Cut112]
FEATURE [Part::Cylinder] Cylinder102  label="center-Cylinder039"
  Angle = 360
  AttacherType = Attacher::AttachEngine3D
  Height = 10
  Placement = pos=(0,0,5) rot=(0,0,1;0rad)
  Radius = 6
FEATURE [Part::Cylinder] Cylinder103  label="center-Cylinder040"
  Angle = 360
  AttacherType = Attacher::AttachEngine3D
  Height = 10
  Placement = pos=(0,0,5) rot=(0,0,1;0rad)
  Radius = 15
FEATURE [Part::Cylinder] Cylinder105
  Angle = 360
  AttacherType = Attacher::AttachEngine3D
  Height = 10
  Placement = pos=(0,0,-14) rot=(0,0,1;0rad)
  Radius = 3
FEATURE [Part::Cylinder] Cylinder106
  Angle = 360
  AttacherType = Attacher::AttachEngine3D
  Height = 6
  Placement = pos=(0,0,-4) rot=(0,0,1;0rad)
  Radius = 9
FEATURE [Part::Cylinder] Cylinder107
  Angle = 360
  AttacherType = Attacher::AttachEngine3D
  Height = 10
  Radius = 9
FEATURE [Part::Cylinder] Cylinder108
  Angle = 360
  AttacherType = Attacher::AttachEngine3D
  Height = 10
  Placement = pos=(0,0,-14) rot=(0,0,1;0rad)
  Radius = 3
FEATURE [Part::Cylinder] Cylinder109
  Angle = 360
  AttacherType = Attacher::AttachEngine3D
  Height = 10
  Placement = pos=(0,0,-14) rot=(0,0,1;0rad)
  Radius = 9
FEATURE [Part::Cylinder] Cylinder110
  Angle = 360
  AttacherType = Attacher::AttachEngine3D
  Height = 10
  Radius = 14
FEATURE [Part::Cut] Cut115
  Base = -> Cylinder110
  Placement = pos=(0,0,-4) rot=(0,0,1;0rad)
  Tool = -> Cylinder107
FEATURE [Part::Cylinder] Cylinder111
  Angle = 360
  AttacherType = Attacher::AttachEngine3D
  Height = 10
  Placement = pos=(0,0,-14) rot=(0,0,1;0rad)
  Radius = 5
FEATURE [Part::Cut] Cut116
  Base = -> Cylinder109
  Tool = -> Cylinder105
FEATURE [Part::RegularPolygon] RegularPolygon008  label="Regular polygon008"
  AttacherType = Attacher::AttachEngine3D
  Circumradius = 6
  Polygon = 6
FEATURE [Part::Extrusion] Extrude011  label="hex-head008"
  Base = -> RegularPolygon008
  Dir = (0,0,1)
  DirMode = 2
  FaceMakerClass = Part::FaceMakerBullseye
  LengthFwd = 6
  LengthRev = 0
  Placement = pos=(0,0,-4) rot=(0,0,1;0rad)
  Solid = true
  Symmetric = false
FEATURE [Part::Cut] Cut117
  Base = -> Cylinder111
  Placement = pos=(0,0,-10) rot=(0,0,1;0rad)
  Tool = -> Cylinder108
FEATURE [Part::Cut] Cut118
  Base = -> Cylinder106
  Tool = -> Extrude011
FEATURE [Part::MultiFuse] Fusion032
  Shapes = -> [Cut118,Cut115,Cut116,Cut117]
FEATURE [App::DocumentObjectGroup] Group015  label="shaft-extender"
  Group = -> [Fusion032]
FEATURE [Part::Cylinder] Cylinder104  label="center-Cylinder041"
  Angle = 360
  AttacherType = Attacher::AttachEngine3D
  Height = 7
  Placement = pos=(0,0,8) rot=(0,0,1;0rad)
  Radius = 11
FEATURE [Part::Cut] Cut113
  Base = -> Cylinder103
  Tool = -> Cylinder104
FEATURE [Part::Cut] Cut114
  Base = -> Cut113
  Placement = pos=(0,0,0) rot=(0,1,0;1.5708rad)
  Tool = -> Cylinder102
FEATURE [Part::Cylinder] Cylinder112
  Angle = 360
  AttacherType = Attacher::AttachEngine3D
  Height = 30
  Placement = pos=(-23,0,-2) rot=(0,0,1;0rad)
  Radius = 28
FEATURE [Part::Cylinder] Cylinder113
  Angle = 360
  AttacherType = Attacher::AttachEngine3D
  Height = 30
  Placement = pos=(-23,0,-2) rot=(0,0,1;0rad)
  Radius = 33
FEATURE [Part::Cut] Cut119
  Base = -> Cylinder113
  Tool = -> Cylinder112
FEATURE [Part::Cylinder] Cylinder114  label="center-Cylinder042"
  Angle = 360
  AttacherType = Attacher::AttachEngine3D
  Height = 7
  Placement = pos=(0,0,8) rot=(0,0,1;0rad)
  Radius = 11
FEATURE [Part::Cylinder] Cylinder115  label="center-Cylinder043"
  Angle = 360
  AttacherType = Attacher::AttachEngine3D
  Height = 38
  Placement = pos=(0,0,-9) rot=(0,0,1;0rad)
  Radius = 6
FEATURE [Part::MultiFuse] Fusion033
  Placement = pos=(0,0,0) rot=(0,1,0;1.5708rad)
  Shapes = -> [Cylinder114,Cylinder115]
FEATURE [Part::MultiFuse] Fusion034
  Shapes = -> [Cut119,Cut114]
FEATURE [Part::Cut] Cut120
  Base = -> Fusion034
  Tool = -> Fusion033
FEATURE [App::DocumentObjectGroup] Group014  label="shaft-secure"
  Group = -> [Cut120]
